# Revit family: Air Source 250
name_source: partatom
category: Mechanical Equipment
revit_build: Autodesk Revit 2017 (Build: 20190507_1515(x64)
units: mm (PartAtom-declared; Revit-internal decimal feet)

## family parameters
Always vertical = Yes
Cut with Voids When Loaded = No
Part Type = Normal
Room Calculation Point = No
Round Connector Dimension = Use Diameter
Shared = No
Work Plane-Based = No

## types (2) — shared parameters
208V-230V/1PH/60HZ MCA = -
208V-230V/1PH/60HZ MOCP = -
208V-230V/1PH/60HZ RLA = -
440V-480V/3PH/60HZ MOCP = 70
575V/3PH/60HZ MOCP = 60
Air Volume (CFM) = 8,000
BTUH Cooling = 218,000
BTUH Heating = 272,450
CONDENSATE CONN SIZE = 2"
Clearance Back = 36"
Clearance Front = 36"
Clearance Left = 36"
Clearance Right = 24"
Compressor Type = Piston
Condensate from Bottom = 16"
Condensate from Left = 5 1/2"
Description = Air Source Heat Pump Water Heater
Evap Bottom from Bottom = 37"
Evap Left from Left = 73 3/4"
Evap Right from Left = 10 7/8"
Evap Top from Bottom = 64 1/2"
FLOW RATE (GPM) = 50
Fan Inner Dia = 27 3/8"
Fan Outer Dia = 29"
Lbs.R134a = 50
Manufacturer = Lochinvar
SES BIM Studio # = 21 0649 02
UNIT LENGTH = 84 5/8"
UNIT WIDTH = 54 3/8"
URL = https://www.lochinvar.com
Unit Top Panel Depth = 1 5/8"
WATER CONN SIZE = 2"
WEIGHT = 2,175
Water In from Bottom = 9 1/2"
Water Out from Bottom = 26 1/2"
Water from Left = 75 1/2"

## per-type parameters (varying)
| type | 208V-230V/3PH/60HZ MCA | 208V-230V/3PH/60HZ MOCP | 208V-230V/3PH/60HZ RLA | 440V-480V/3PH/60HZ MCA | 440V-480V/3PH/60HZ RLA | 575V/3PH/60HZ MCA | 575V/3PH/60HZ RLA | Blowers | Fan/Blower Depth | Fans | Model | UNIT HEIGHT |
| 250 Axial | 119 | 125 | 95.4 | 60 | 49.1 | 50 | 40.9 | No | 3 7/8" | Yes |  | 70" |
| 250 Blower | 129 | 150 | 106.2 | 65 | 52.8 | 54 | 44.2 | Yes | 1 5/8" | No | AHP250 | 67 3/4" |

## geometry (parser evidence)
native form markers: Sweep x2
no freeform markers — native parametric forms only
